# Revit family: 206_Universal-tiililapivienti
name_source: partatom
category: Duct Accessories
units: mm (PartAtom-declared; Revit-internal decimal feet)

## family parameters
Always vertical = Yes
Cut with Voids When Loaded = No
Part Type = Breaks Into
Round Connector Dimension = Use Diameter
Shared = No
Work Plane-Based = No

## types (1)
- VILPE UNIVERSAL TILE PASS-THROUGH
    CAT0 = Yes
    D = 110 mm
    Description = Pass-through seal
    ET = 2 mm  [stored 0.00656168 ft]
    H2 = 56 mm  [stored 0.183727 ft]
    H2D = 532 mm  [stored 1.74541 ft]
    L = 595 mm  [stored 1.9521 ft]
    L2D = 10 mm  [stored 0.0328084 ft]
    L3 = 532 mm  [stored 1.74541 ft]
    L32 = 254 mm
    LL3 = 395 mm  [stored 1.29593 ft]
    LL32 = 793 mm
    LLL = 298 mm
    L__ve = -595 mm  [stored -1.9521 ft]
    MC Product Code = VILPE UNIVERSAL TILE PASS-THROUGH
    Manufacturer = Vilpe
    QmdConnectorList = 201;D;202;D
    THW = 50 mm  [stored 0.164042 ft]
    URL = http://www.vilpe.com
    W12 = 85 mm  [stored 0.278871 ft]
    W2D = 400 mm  [stored 1.31234 ft]
    W3 = 400 mm  [stored 1.31234 ft]
    W32 = 200 mm  [stored 0.656168 ft]
    WL = 80 mm  [stored 0.262467 ft]
    magiPartTypeId = 206
    magiProductFamilyId = Universal-tiililapivienti
    magiProductId = Universal-tiililapivienti

note: [stored X ft] marks values corroborated as IEEE doubles in the binary element streams (Revit-internal decimal feet)

## geometry (parser evidence)
native form markers: Sweep x2
no freeform markers — native parametric forms only
